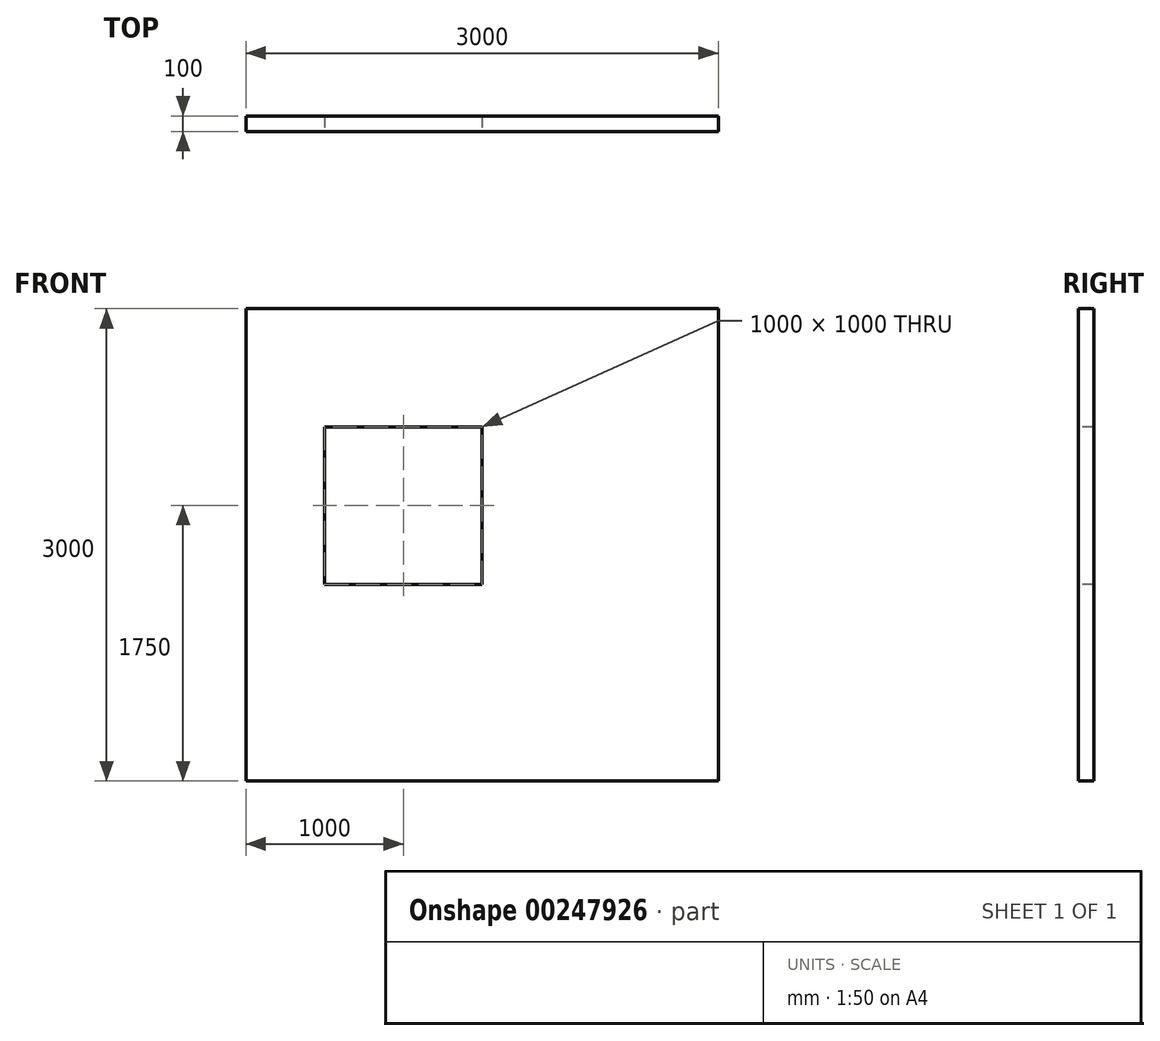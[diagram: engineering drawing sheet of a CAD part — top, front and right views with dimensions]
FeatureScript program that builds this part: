
annotation { "Feature Type Name" : "Feature", "Feature Type Description" : "" }
export const myFeature = defineFeature(function(context is Context, id is Id, definition is map)
    precondition{}
    {
        {
            var Q0;
            Q0=qCreatedBy(makeId("Front.planeOp"),FACE);
            var sketch = newSketch(context, id + "F0", { "sketchPlane" : qUnion([Q0])});
            skLineSegment(sketch, "E0.bottom", {"start": v(1500, 0) * mm, "end": v(-1500, 0) * mm});
            skLineSegment(sketch, "E0.top", {"start": v(1500, 3000) * mm, "end": v(-1500, 3000) * mm});
            skLineSegment(sketch, "E0.left", {"start": v(1500, 0) * mm, "end": v(1500, 3000) * mm});
            skLineSegment(sketch, "E0.right", {"start": v(-1500, 0) * mm, "end": v(-1500, 3000) * mm});
            skPoint(sketch, "E0.middle", {"position": v(0, 1500) * mm});
            skSolve(sketch);
        }
        {
            var Q0;
            Q0=makeQuery(id+"F0.imprint","IMPRINT",FACE,{"disambiguationData":[TD([[makeQuery(id+"F0.imprint","IMPRINT",EDGE,{"derivedFrom":sQuery(id+"F0.wireOp",EDGE,"E0.bottom")}),-1.0]])]});
            extrude(context, id + "F1", {"entities" : qUnion([Q0]), "endBound" : BoundingType.SYMMETRIC, "depth" : 100 * mm});
        }
        {
            var Q0;
            Q0=makeQuery(id+"F1.opExtrude","CAP_FACE",FACE,{"disambiguationData":[OSD([sQuery(id+"F0.wireOp",EDGE,"E0.bottom"),sQuery(id+"F0.wireOp",EDGE,"E0.top"),sQuery(id+"F0.wireOp",EDGE,"E0.left"),sQuery(id+"F0.wireOp",EDGE,"E0.right")])],"isStart":false});
            var sketch = newSketch(context, id + "F2", { "sketchPlane" : qUnion([Q0])});
            skLineSegment(sketch, "E1.bottom", {"start": v(0, 1250) * mm, "end": v(-1000, 1250) * mm});
            skLineSegment(sketch, "E1.top", {"start": v(0, 2250) * mm, "end": v(-1000, 2250) * mm});
            skLineSegment(sketch, "E1.left", {"start": v(0, 1250) * mm, "end": v(0, 2250) * mm});
            skLineSegment(sketch, "E1.right", {"start": v(-1000, 1250) * mm, "end": v(-1000, 2250) * mm});
            skPoint(sketch, "E1.middle", {"position": v(-500, 1750) * mm});
            skLineSegment(sketch, "E2", {"start": v(500, 3000) * mm, "end": v(500, 0) * mm, "construction": true});
            skLineSegment(sketch, "E3", {"start": v(-1500, 3000) * mm, "end": v(500, 3000) * mm, "construction": true});
            skPoint(sketch, "E4", {"position": v(-500, 3000) * mm});
            skSolve(sketch);
        }
        {
            var Q0;
            Q0=makeQuery(id+"F2.imprint","IMPRINT",FACE,{"disambiguationData":[TD([[makeQuery(id+"F2.imprint","IMPRINT",EDGE,{"derivedFrom":sQuery(id+"F2.wireOp",EDGE,"E1.bottom")}),-1.0]])]});
            extrude(context, id + "F3", {"entities" : qUnion([Q0]), "operationType" : NewBodyOperationType.REMOVE, "endBound" : BoundingType.THROUGH_ALL, "oppositeDirection" : true, "depth" : 25 * mm});
        }
    });
